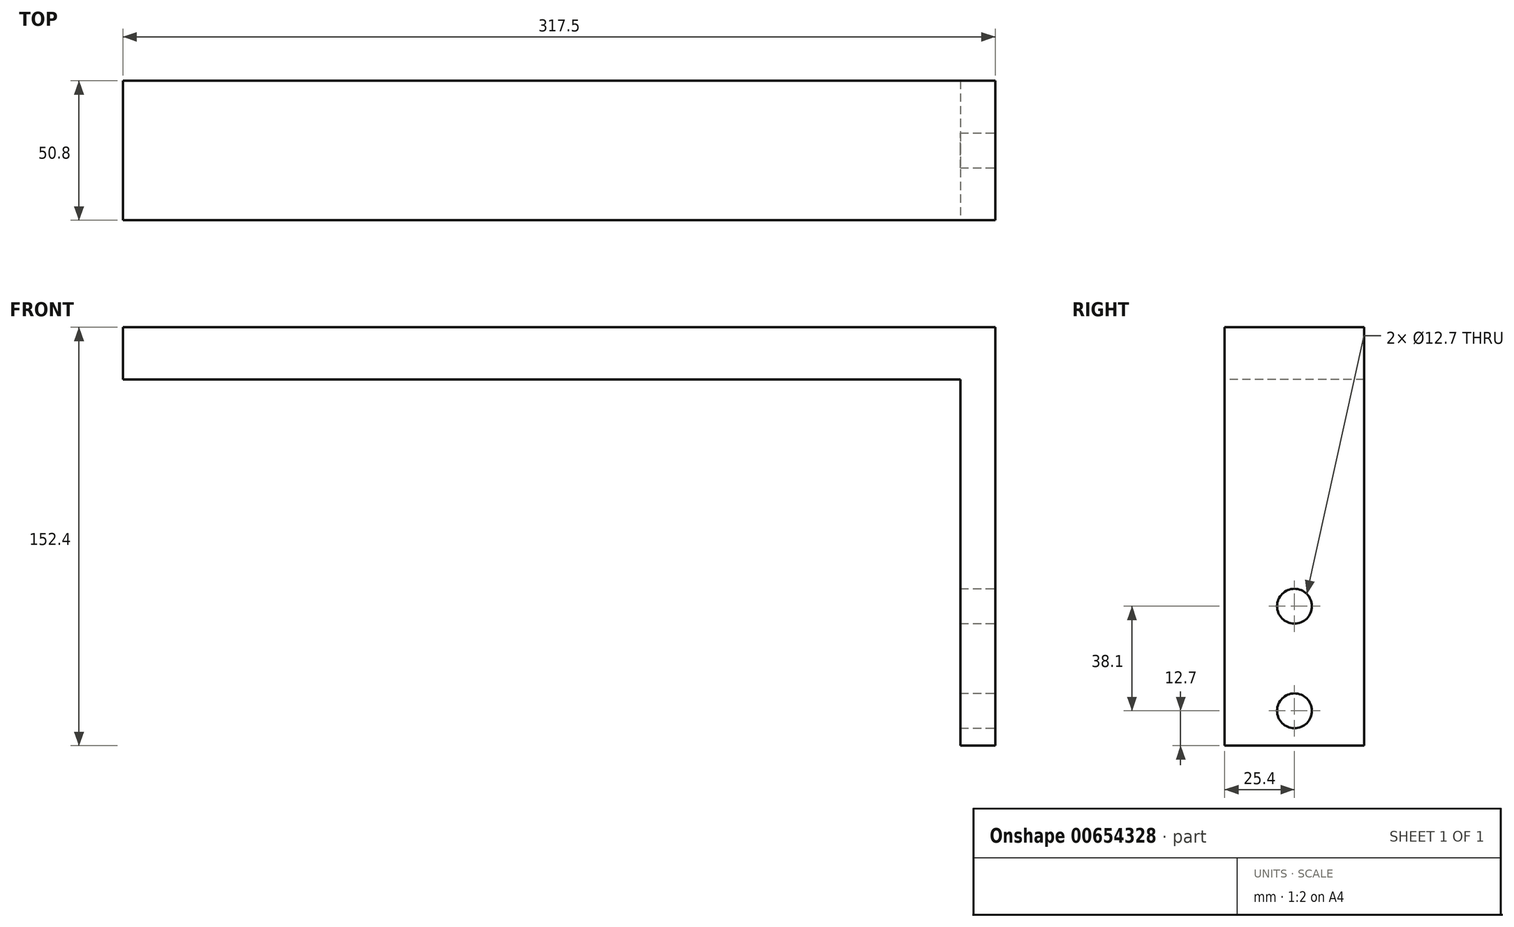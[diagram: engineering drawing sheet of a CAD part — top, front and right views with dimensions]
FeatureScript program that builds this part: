
annotation { "Feature Type Name" : "Feature", "Feature Type Description" : "" }
export const myFeature = defineFeature(function(context is Context, id is Id, definition is map)
    precondition{}
    {
        {
            var Q0;
            Q0=qCreatedBy(makeId("Top.planeOp"),FACE);
            var sketch = newSketch(context, id + "F0", { "sketchPlane" : qUnion([Q0])});
            skLineSegment(sketch, "E0.bottom", {"start": v(152.4, 25.4) * mm, "end": v(-152.4, 25.4) * mm});
            skLineSegment(sketch, "E0.top", {"start": v(152.4, -25.4) * mm, "end": v(-152.4, -25.4) * mm});
            skLineSegment(sketch, "E0.left", {"start": v(152.4, 25.4) * mm, "end": v(152.4, -25.4) * mm});
            skLineSegment(sketch, "E0.right", {"start": v(-152.4, 25.4) * mm, "end": v(-152.4, -25.4) * mm});
            skPoint(sketch, "E0.middle", {"position": v(0, 0) * mm});
            skSolve(sketch);
        }
        {
            var Q0;
            Q0 = qSketchRegion(id + "F0", true);
            extrude(context, id + "F1", {"entities" : qUnion([Q0]), "depth" : 19.05 * mm, "offsetDistance" : 25.4 * mm});
        }
        {
            var Q0;
            Q0=makeQuery(id+"F1.opExtrude","SWEPT_FACE",FACE,{"disambiguationData":[OSD([sQuery(id+"F0.wireOp",EDGE,"E0.left")])]});
            var sketch = newSketch(context, id + "F2", { "sketchPlane" : qUnion([Q0])});
            skLineSegment(sketch, "E1.bottom", {"start": v(-25.4, 19.05) * mm, "end": v(25.4, 19.05) * mm});
            skLineSegment(sketch, "E1.top", {"start": v(-25.4, -133.35) * mm, "end": v(25.4, -133.35) * mm});
            skLineSegment(sketch, "E1.left", {"start": v(-25.4, 19.05) * mm, "end": v(-25.4, -133.35) * mm});
            skLineSegment(sketch, "E1.right", {"start": v(25.4, 19.05) * mm, "end": v(25.4, -133.35) * mm});
            skSolve(sketch);
        }
        {
            var Q0;
            Q0 = qSketchRegion(id + "F2", true);
            extrude(context, id + "F3", {"entities" : qUnion([Q0]), "operationType" : NewBodyOperationType.ADD, "depth" : 12.7 * mm, "offsetDistance" : 25.4 * mm});
        }
        {
            var Q0;
            Q0=makeQuery(id+"F3.opExtrude","CAP_FACE",FACE,{"disambiguationData":[OSD([sQuery(id+"F2.wireOp",EDGE,"E1.bottom"),sQuery(id+"F2.wireOp",EDGE,"E1.top"),sQuery(id+"F2.wireOp",EDGE,"E1.left"),sQuery(id+"F2.wireOp",EDGE,"E1.right")])],"isStart":false});
            var sketch = newSketch(context, id + "F4", { "sketchPlane" : qUnion([Q0])});
            skCircle(sketch, "E2", {"center": v(0, -120.65) * mm, "radius": 6.35 * mm});
            skPoint(sketch, "E2.centerSnap0", {"position": v(0, -133.35) * mm});
            skCircle(sketch, "E3", {"center": v(0, -82.55) * mm, "radius": 6.35 * mm});
            skSolve(sketch);
        }
        {
            var Q0;
            Q0 = qSketchRegion(id + "F4", true);
            extrude(context, id + "F5", {"entities" : qUnion([Q0]), "operationType" : NewBodyOperationType.REMOVE, "endBound" : BoundingType.UP_TO_NEXT, "oppositeDirection" : true, "depth" : 25.4 * mm, "offsetDistance" : 25.4 * mm});
        }
    });
